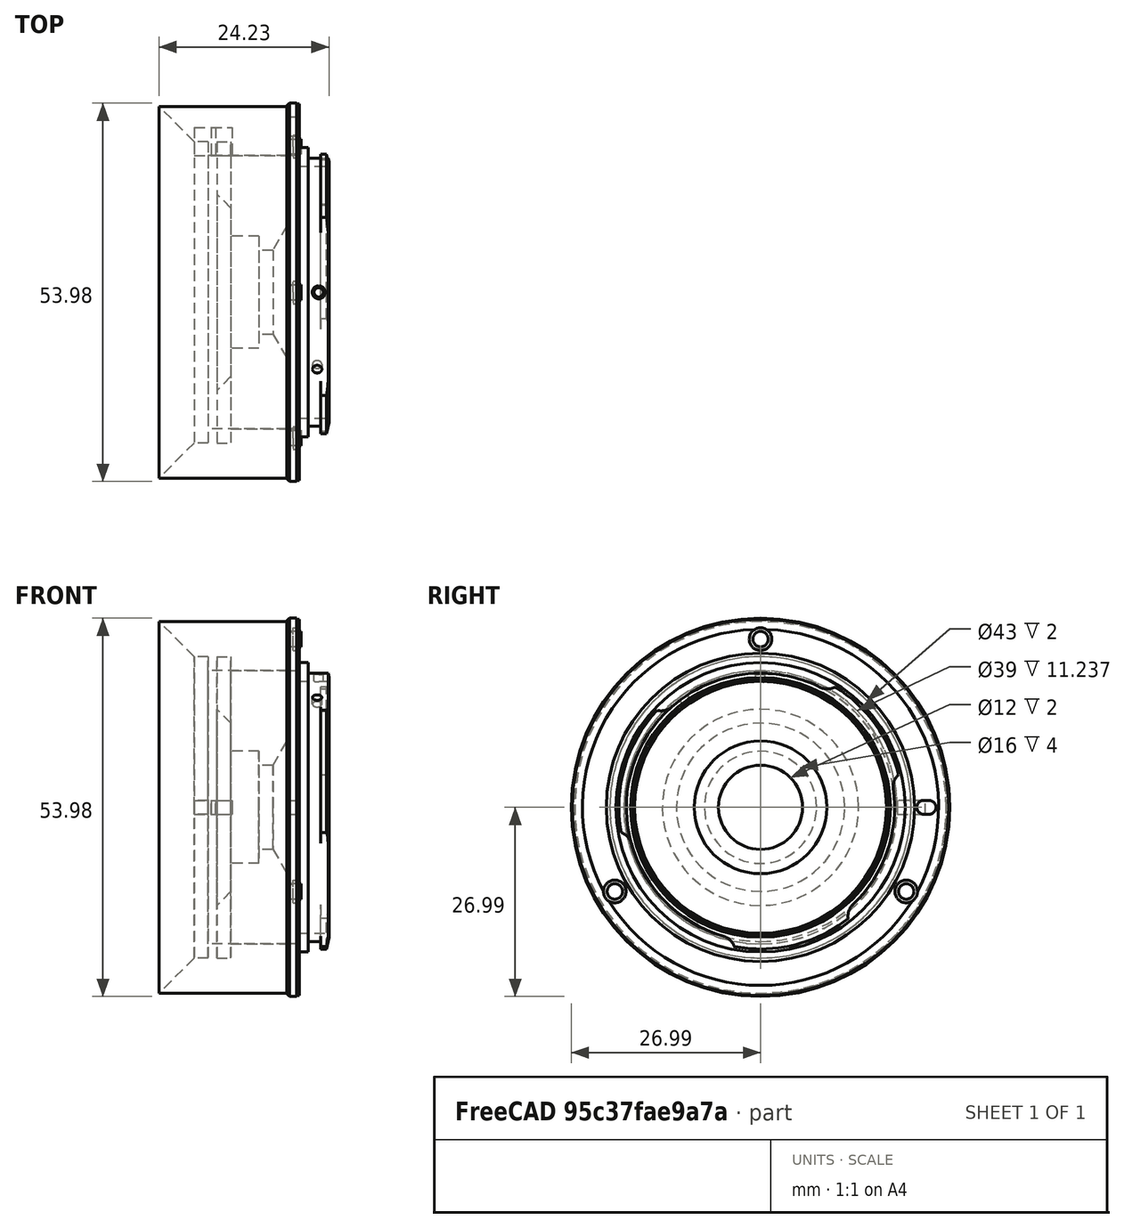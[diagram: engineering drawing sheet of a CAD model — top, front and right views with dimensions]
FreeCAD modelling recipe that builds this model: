
FCSTD DOCUMENT  (FreeCAD 0.20R29410 (Git))
Label: FUJIQUICKSNAP
License: All rights reserved
LicenseURL: http://en.wikipedia.org/wiki/All_rights_reserved
objects: TechDraw::DrawViewDimension×27, TechDraw::DrawProjGroupItem×6, TechDraw::DrawHatch×6, Sketcher::SketchObject×5, PartDesign::Body×4, PartDesign::Pad×3, PartDesign::Revolution×2, PartDesign::Boolean×2, App::Part×2, TechDraw::DrawProjGroup×2, TechDraw::DrawViewSection×2, TechDraw::DrawViewAnnotation×2, Spreadsheet::Sheet×1, Part::Feature×1, TechDraw::DrawSVGTemplate×1, TechDraw::DrawViewSpreadsheet×1, TechDraw::DrawPage×1
note: 22 computed .brp shape members not serialized (recipe doc carries the construction recipe); baked Part::Feature solids carry a one-line shape summary decoded from their .brp

FEATURE [Spreadsheet::Sheet] Spreadsheet
  cells = A2=Focal length; B2(f)=32; C2=Mount inner radius; D2(MIR)==19.5mm; A3=Aperture; B3(Fstop)=10; C3=Mount outer radius; D3(MOR)==26.5mm; A4=Hyperfocal; B4(HFD)==B2 ^ 2 / (B3 / 30); C4=Lens support radius; D4(LSR)==8mm; A5=Lens to sensor; B5(L2S)==1 / (1 / B2 - 1 / B4); C5=Lens support depth; D5(LSD)==4mm; A6=FFD; B6(FFD)==19.25 + 1.85; A7=Mount to lens; B7(M2L)==B5 - B6
FEATURE [Sketcher::SketchObject] Sketch
  FullyConstrained = true
  MapMode = 5
  Support = -> [XY_Plane001]
  expr: Constraints[17] = Spreadsheet.M2L
  expr: Constraints[7] = Spreadsheet.MIR
  expr: Constraints[8] = Spreadsheet.MOR
  sketch-geometry (6):
    g0: LineSegment StartX=-18.2368 StartY=26.5 StartZ=0 EndX=0 EndY=26.5 EndZ=0
    g1: LineSegment StartX=0 StartY=26.5 StartZ=0 EndX=0 EndY=19.5 EndZ=0
    g2: LineSegment StartX=-13.2368 StartY=21.5 StartZ=0 EndX=-18.2368 EndY=26.5 EndZ=0
    g3: LineSegment StartX=0 StartY=19.5 StartZ=0 EndX=-11.2368 EndY=19.5 EndZ=0
    g4: LineSegment StartX=-11.2368 StartY=19.5 StartZ=0 EndX=-11.2368 EndY=21.5 EndZ=0
    g5: LineSegment StartX=-11.2368 StartY=21.5 StartZ=0 EndX=-13.2368 EndY=21.5 EndZ=0
  constraints (18):
    c: Coincident(g0,g1)
    c: Coincident(g1,g3)
    c: Coincident(g5,g2)
    c: Coincident(g2,g0)
    c: Horizontal(g0)
    c: Vertical(g1)
    c: PointOnObject(g1,g-2)
    c: DistanceY(g-1,g1) = 19.5
    c: DistanceY(g-1,g0) = 26.5
    c: Coincident(g3,g4)
    c: Horizontal(g3)
    c: Coincident(g4,g5)
    c: Horizontal(g5)
    c: Vertical(g4)
    c: Angle(g5,g2) = 2.35619
    c: Distance(g5) = 2
    c: Distance(g4) = 2
    c: DistanceX(g3,g1) = 11.2368
FEATURE [PartDesign::Revolution] Revolution
  Angle = 360
  Axis = (1,0,0)
  Base = (0,0,0)
  Profile = -> Sketch
  ReferenceAxis = -> Sketch [H_Axis]
FEATURE [Sketcher::SketchObject] Sketch001
  FullyConstrained = true
  MapMode = 5
  Support = -> [XY_Plane003]
  expr: Constraints[18] = Spreadsheet.MIR
  expr: Constraints[23] = Spreadsheet.LSR
  expr: Constraints[27] = Spreadsheet.LSD
  expr: Constraints[28] = Constraints[26] + Constraints[27]
  sketch-geometry (11):
    g0: LineSegment StartX=-8 StartY=19.5 StartZ=0 EndX=0 EndY=19.5 EndZ=0
    g1: LineSegment StartX=0 StartY=19.5 StartZ=0 EndX=0 EndY=9.4641 EndZ=0
    g2: LineSegment StartX=-8 StartY=21.5 StartZ=0 EndX=-8 EndY=19.5 EndZ=0
    g3: LineSegment StartX=-10 StartY=21.5 StartZ=0 EndX=-8 EndY=21.5 EndZ=0
    g4: LineSegment StartX=-10 StartY=14 StartZ=0 EndX=-10 EndY=21.5 EndZ=0
    g5: LineSegment StartX=-8 StartY=8 StartZ=0 EndX=-8 EndY=12 EndZ=0
    g6: LineSegment StartX=-8 StartY=12 StartZ=0 EndX=-10 EndY=14 EndZ=0
    g7: LineSegment StartX=-4 StartY=8 StartZ=0 EndX=-8 EndY=8 EndZ=0
    g8: LineSegment StartX=-4 StartY=6 StartZ=0 EndX=-4 EndY=8 EndZ=0
    g9: LineSegment StartX=0 StartY=9.4641 StartZ=0 EndX=-2 EndY=6 EndZ=0
    g10: LineSegment StartX=-2 StartY=6 StartZ=0 EndX=-4 EndY=6 EndZ=0
  constraints (33):
    c: Coincident(g0,g1)
    c: Coincident(g1,g9)
    c: Coincident(g7,g5)
    c: Coincident(g2,g0)
    c: Horizontal(g0)
    c: Vertical(g1)
    c: PointOnObject(g1,g-2)
    c: Coincident(g3,g2)
    c: Vertical(g2)
    c: Coincident(g4,g3)
    c: Horizontal(g3)
    c: DistanceY(g2,g2) = 2
    c: Coincident(g6,g4)
    c: Vertical(g4)
    c: Coincident(g5,g6)
    c: Vertical(g5)
    c: DistanceX(g3,g3) = 2
    c: Angle(g6,g4) = 2.35619
    c: DistanceY(g-1,g0) = 19.5
    c: DistanceY(g5,g5) = 4
    c: Coincident(g8,g7)
    c: Horizontal(g7)
    c: Coincident(g10,g8)
    c: DistanceY(g-1,g7) = 8
    c: Vertical(g8)
    c: DistanceY(g8,g8) = 2
    c: DistanceX(g10,g9) = 4
    c: DistanceX(g7,g7) = 4
    c: DistanceX(g0,g0) = 8
    c: Coincident(g9,g10)
    c: Horizontal(g10)
    c: Angle(g1,g9) = 2.61799
    c: DistanceX(g10,g10) = 2
FEATURE [PartDesign::Revolution] Revolution001
  Angle = 360
  Axis = (1,0,0)
  Base = (0,0,0)
  Profile = -> Sketch001
  ReferenceAxis = -> Sketch001 [H_Axis]
FEATURE [Part::Feature] Solid  label="u43 lens mount"
  Placement = pos=(0,0,0) rot=(0,0,1;4.71239rad)
  shape: bbox 5.994 x 53.98 x 53.98 mm, 69 faces (baked)
FEATURE [Sketcher::SketchObject] Sketch002
  FullyConstrained = true
  MapMode = 5
  Placement = pos=(0,0,0) rot=(0.57735,0.57735,0.57735;2.0944rad)
  Support = -> [YZ_Plane001]
  expr: Constraints[7] = 2 * 24 * cos(30)
  expr: Constraints[8] = 2 * 24 * cos(30)
  sketch-geometry (3):
    g0: Circle CenterX=-20.7846 CenterY=-12 CenterZ=0 NormalX=0 NormalY=0 NormalZ=1 AngleXU=0 Radius=1.1
    g1: Circle CenterX=20.7846 CenterY=-12 CenterZ=0 NormalX=0 NormalY=0 NormalZ=1 AngleXU=0 Radius=1.1
    g2: Circle CenterX=0 CenterY=24 CenterZ=0 NormalX=0 NormalY=0 NormalZ=1 AngleXU=0 Radius=1.1
  constraints (9):
    c: PointOnObject(g2,g-2)
    c: DistanceY(g-1,g2) = 24
    c: Radius(g0) = 1.1
    c: Equal(g0,g1)
    c: Equal(g1,g2)
    c: Distance(g-1,g0) = 24
    c: Distance(g-1,g1) = 24
    c: DistanceX(g0,g1) = 41.5692
    c: Distance(g1,g2) = 41.5692
FEATURE [PartDesign::Pad] Pad
  BaseFeature = -> Revolution
  Direction = (1,-2e-16,3e-16)
  Length = 2
  Length2 = 10
  Profile = -> Sketch002
  ReferenceAxis = -> Sketch002 [N_Axis]
  Type = 0
FEATURE [Sketcher::SketchObject] Sketch003
  FullyConstrained = true
  MapMode = 5
  Placement = pos=(0,0,0) rot=(0.57735,0.57735,0.57735;2.0944rad)
  Support = -> [YZ_Plane004]
  expr: Constraints[14] = Spreadsheet.MIR
  sketch-geometry (5):
    g0: LineSegment StartX=23.5 StartY=1 StartZ=0 EndX=19.5 EndY=1 EndZ=0
    g1: LineSegment StartX=19.5 StartY=-1 StartZ=0 EndX=23.5 EndY=-1 EndZ=0
    g2: LineSegment StartX=23.5 StartY=-1 StartZ=0 EndX=23.5 EndY=1 EndZ=0
    g3: LineSegment StartX=19.5 StartY=1 StartZ=0 EndX=19.5 EndY=0 EndZ=0
    g4: LineSegment StartX=19.5 StartY=0 StartZ=0 EndX=19.5 EndY=-1 EndZ=0
  constraints (15):
    c: Coincident(g0,g3)
    c: Coincident(g4,g1)
    c: Coincident(g1,g2)
    c: Coincident(g2,g0)
    c: Horizontal(g0)
    c: Horizontal(g1)
    c: Vertical(g2)
    c: Coincident(g3,g4)
    c: Vertical(g3)
    c: Vertical(g4)
    c: PointOnObject(g3,g-1)
    c: Equal(g3,g4)
    c: DistanceY(g2,g2) = 2
    c: DistanceX(g0,g0) = 4
    c: DistanceX(g-1,g3) = 19.5
FEATURE [PartDesign::Pad] Pad001
  Direction = (1,-2e-16,3e-16)
  Length = 3
  Length2 = 10
  Placement = pos=(0,0,0) rot=(0.57735,0.57735,0.57735;2.0944rad)
  Profile = -> Sketch003
  ReferenceAxis = -> Sketch003 [N_Axis]
  Type = 0
FEATURE [PartDesign::Body] Body002
  Group = -> [Sketch003,Pad001]
  Origin = -> Origin004
  Placement = pos=(-13.2,0,0) rot=(0,0,1;0rad)
  Tip = -> Pad001
FEATURE [Sketcher::SketchObject] Sketch004
  FullyConstrained = true
  MapMode = 5
  Placement = pos=(0,0,0) rot=(0.57735,0.57735,0.57735;2.0944rad)
  Support = -> [YZ_Plane005]
  expr: Constraints[14] = Spreadsheet.MIR
  sketch-geometry (5):
    g0: LineSegment StartX=23.5 StartY=1 StartZ=0 EndX=19.5 EndY=1 EndZ=0
    g1: LineSegment StartX=19.5 StartY=-1 StartZ=0 EndX=23.5 EndY=-1 EndZ=0
    g2: LineSegment StartX=23.5 StartY=-1 StartZ=0 EndX=23.5 EndY=1 EndZ=0
    g3: LineSegment StartX=19.5 StartY=1 StartZ=0 EndX=19.5 EndY=0 EndZ=0
    g4: LineSegment StartX=19.5 StartY=0 StartZ=0 EndX=19.5 EndY=-1 EndZ=0
  constraints (15):
    c: Coincident(g0,g3)
    c: Coincident(g4,g1)
    c: Coincident(g1,g2)
    c: Coincident(g2,g0)
    c: Horizontal(g0)
    c: Horizontal(g1)
    c: Vertical(g2)
    c: Coincident(g3,g4)
    c: Vertical(g3)
    c: Vertical(g4)
    c: PointOnObject(g3,g-1)
    c: Equal(g3,g4)
    c: DistanceY(g2,g2) = 2
    c: DistanceX(g0,g0) = 4
    c: DistanceX(g-1,g3) = 19.5
FEATURE [PartDesign::Pad] Pad002
  Direction = (1,-2e-16,3e-16)
  Length = 3
  Length2 = 10
  Placement = pos=(0,0,0) rot=(0.57735,0.57735,0.57735;2.0944rad)
  Profile = -> Sketch004
  ReferenceAxis = -> Sketch004 [N_Axis]
  Type = 0
FEATURE [PartDesign::Body] Body003
  Group = -> [Sketch004,Pad002]
  Origin = -> Origin005
  Placement = pos=(-10.8,0,0) rot=(0,0,1;0rad)
  Tip = -> Pad002
FEATURE [PartDesign::Boolean] Boolean
  BaseFeature = -> Pad
  Group = -> [Body002]
  Type = 0
FEATURE [PartDesign::Body] Body
  Group = -> [Sketch,Revolution,Sketch002,Pad,Boolean]
  Origin = -> Origin001
  Tip = -> Boolean
FEATURE [App::Part] Part  label="Tube"
  Group = -> [Body]
  Origin = -> Origin
FEATURE [PartDesign::Boolean] Boolean001
  BaseFeature = -> Revolution001
  Group = -> [Body003]
  Type = 1
FEATURE [PartDesign::Body] Body001
  Group = -> [Sketch001,Revolution001,Boolean001]
  Origin = -> Origin003
  Tip = -> Boolean001
FEATURE [App::Part] Part001  label="Cap"
  Group = -> [Body001]
  Origin = -> Origin002
  Placement = pos=(-3.3,0,0) rot=(0,0,1;0rad)
FEATURE [TechDraw::DrawSVGTemplate] Template
  EditableTexts = AUTHOR_NAME=monke; DN=1; DRAWING_TITLE=QUICKSNAP TO µ4/3; FC-DATE=17/09/2022; FC-REV=REV A; FC-SC=SCALE; FC-SH=1/1; FC-SI=A4; FreeCAD_DRAWING=1.85mm thick µ4/3 mount not included; PN=1; SI-1=Units in millimeter
  Height = 210
  Orientation = 1
  Width = 297
FEATURE [TechDraw::DrawProjGroupItem] ProjItem  label="Front"
  CoarseView = false
  Direction = (-1,0,0)
  Focus = 100
  HardHidden = false
  IsoCount = 0
  IsoHidden = false
  IsoVisible = false
  LockPosition = true
  Perspective = false
  Rotation = 0
  RotationVector = (0,1,0)
  ScaleType = 2
  SeamHidden = false
  SeamVisible = true
  SmoothHidden = false
  SmoothVisible = true
  Source = -> [Part001]
  Type = 0
  X = 0
  XDirection = (0,-1,2e-16)
  Y = 0
FEATURE [TechDraw::DrawProjGroupItem] ProjItem003  label="Bottom"
  CoarseView = false
  Direction = (0,-2e-16,-1)
  Focus = 100
  HardHidden = false
  IsoCount = 0
  IsoHidden = false
  IsoVisible = false
  LockPosition = false
  Perspective = false
  Rotation = 0
  RotationVector = (1,0,0)
  ScaleType = 2
  SeamHidden = false
  SeamVisible = true
  SmoothHidden = false
  SmoothVisible = true
  Source = -> [Part001]
  Type = 5
  X = 0
  XDirection = (0,-1,2e-16)
  Y = -48
FEATURE [TechDraw::DrawProjGroupItem] ProjItem004  label="Rear"
  CoarseView = false
  Direction = (1,0,0)
  Focus = 100
  HardHidden = false
  IsoCount = 0
  IsoHidden = false
  IsoVisible = false
  LockPosition = false
  Perspective = false
  Rotation = 0
  RotationVector = (1,0,0)
  ScaleType = 2
  SeamHidden = false
  SeamVisible = true
  SmoothHidden = false
  SmoothVisible = true
  Source = -> [Part001]
  Type = 3
  X = 47.9767
  XDirection = (0,1,-2e-16)
  Y = 0
FEATURE [TechDraw::DrawProjGroup] ProjGroup
  Anchor = -> ProjItem
  AutoDistribute = true
  LockPosition = false
  ProjectionType = 1
  Rotation = 0
  Scale = 1.5
  ScaleType = 0
  Source = -> [Part001]
  Views = -> [ProjItem,ProjItem003,ProjItem004]
  X = 41.5078
  Y = 159.868
  spacingX = 5
  spacingY = 5
FEATURE [TechDraw::DrawViewDimension] Dimension
  AngleOverride = false
  Arbitrary = false
  ArbitraryTolerances = false
  EqualTolerance = true
  ExtensionAngle = 0
  FormatSpec = ⌀%.2w
  FormatSpecOverTolerance = %+.2w
  FormatSpecUnderTolerance = %+.2w
  Inverted = false
  LineAngle = 0
  LockPosition = false
  MeasureType = 1
  OverTolerance = 0
  References2D = -> [ProjItem004]
  Rotation = 0
  ScaleType = 0
  TheoreticalExact = false
  Type = 5
  UnderTolerance = 0
  X = 10.6396
  Y = -6.61379
FEATURE [TechDraw::DrawViewDimension] Dimension001
  AngleOverride = false
  Arbitrary = false
  ArbitraryTolerances = false
  EqualTolerance = true
  ExtensionAngle = 0
  FormatSpec = ⌀%.2w
  FormatSpecOverTolerance = %+.2w
  FormatSpecUnderTolerance = %+.2w
  Inverted = false
  LineAngle = 0
  LockPosition = false
  MeasureType = 1
  OverTolerance = 0
  References2D = -> [ProjItem004]
  Rotation = 0
  ScaleType = 0
  TheoreticalExact = false
  Type = 5
  UnderTolerance = 0
  X = 28.1565
  Y = -4.45712
FEATURE [TechDraw::DrawViewDimension] Dimension002
  AngleOverride = false
  Arbitrary = false
  ArbitraryTolerances = false
  EqualTolerance = true
  ExtensionAngle = 0
  FormatSpec = ⌀%.2w
  FormatSpecOverTolerance = %+.2w
  FormatSpecUnderTolerance = %+.2w
  Inverted = false
  LineAngle = 0
  LockPosition = false
  MeasureType = 1
  OverTolerance = 0
  References2D = -> [ProjItem004]
  Rotation = 0
  ScaleType = 0
  TheoreticalExact = false
  Type = 5
  UnderTolerance = 0
  X = 10.5917
  Y = 26.4552
FEATURE [TechDraw::DrawViewDimension] Dimension003
  AngleOverride = false
  Arbitrary = false
  ArbitraryTolerances = false
  EqualTolerance = true
  ExtensionAngle = 0
  FormatSpec = ⌀%.2w
  FormatSpecOverTolerance = %+.2w
  FormatSpecUnderTolerance = %+.2w
  Inverted = false
  LineAngle = 0
  LockPosition = false
  MeasureType = 1
  OverTolerance = 0
  References2D = -> [ProjItem004]
  Rotation = 0
  ScaleType = 0
  TheoreticalExact = false
  Type = 5
  UnderTolerance = 0
  X = 18.3317
  Y = 23.0764
FEATURE [TechDraw::DrawViewDimension] Dimension004
  AngleOverride = false
  Arbitrary = false
  ArbitraryTolerances = false
  EqualTolerance = true
  ExtensionAngle = 0
  FormatSpec = %.2w
  FormatSpecOverTolerance = %+.2w
  FormatSpecUnderTolerance = %+.2w
  Inverted = false
  LineAngle = 0
  LockPosition = false
  MeasureType = 1
  OverTolerance = 0
  References2D = -> [ProjItem]
  Rotation = 0
  ScaleType = 0
  TheoreticalExact = false
  Type = 1
  UnderTolerance = 0
  X = -15.9193
  Y = 13.2354
FEATURE [TechDraw::DrawViewDimension] Dimension005
  AngleOverride = false
  Arbitrary = false
  ArbitraryTolerances = false
  EqualTolerance = true
  ExtensionAngle = 0
  FormatSpec = %.2w
  FormatSpecOverTolerance = %+.2w
  FormatSpecUnderTolerance = %+.2w
  Inverted = false
  LineAngle = 0
  LockPosition = false
  MeasureType = 1
  OverTolerance = 0
  References2D = -> [ProjItem]
  Rotation = 0
  ScaleType = 0
  TheoreticalExact = false
  Type = 1
  UnderTolerance = 0
  X = -3.54512
  Y = 21.0953
FEATURE [TechDraw::DrawViewDimension] Dimension006
  AngleOverride = false
  Arbitrary = false
  ArbitraryTolerances = false
  EqualTolerance = true
  ExtensionAngle = 0
  FormatSpec = %.2w
  FormatSpecOverTolerance = %+.2w
  FormatSpecUnderTolerance = %+.2w
  Inverted = false
  LineAngle = 0
  LockPosition = false
  MeasureType = 1
  OverTolerance = 0
  References2D = -> [ProjItem]
  Rotation = 0
  ScaleType = 0
  TheoreticalExact = false
  Type = 1
  UnderTolerance = 0
  X = -14.8124
  Y = -5.64743
FEATURE [TechDraw::DrawViewDimension] Dimension007
  AngleOverride = false
  Arbitrary = false
  ArbitraryTolerances = false
  EqualTolerance = true
  ExtensionAngle = 0
  FormatSpec = %.2w
  FormatSpecOverTolerance = %+.2w
  FormatSpecUnderTolerance = %+.2w
  Inverted = false
  LineAngle = 0
  LockPosition = false
  MeasureType = 1
  OverTolerance = 0
  References2D = -> [ProjItem003]
  Rotation = 0
  ScaleType = 0
  TheoreticalExact = false
  Type = 2
  UnderTolerance = 0
  X = -27.1178
  Y = 9.4377
FEATURE [TechDraw::DrawViewDimension] Dimension008
  AngleOverride = false
  Arbitrary = false
  ArbitraryTolerances = false
  EqualTolerance = true
  ExtensionAngle = 0
  FormatSpec = %.2w
  FormatSpecOverTolerance = %+.2w
  FormatSpecUnderTolerance = %+.2w
  Inverted = false
  LineAngle = 0
  LockPosition = false
  MeasureType = 1
  OverTolerance = 0
  References2D = -> [ProjItem003]
  Rotation = 0
  ScaleType = 0
  TheoreticalExact = false
  Type = 2
  UnderTolerance = 0
  X = -18.1561
  Y = -8.31386
FEATURE [TechDraw::DrawProjGroupItem] ProjItem005  label="Front001"
  CoarseView = false
  Direction = (1,0,0)
  Focus = 100
  HardHidden = false
  IsoCount = 0
  IsoHidden = false
  IsoVisible = false
  LockPosition = true
  Perspective = false
  Rotation = 0
  RotationVector = (0,1,0)
  ScaleType = 2
  SeamHidden = false
  SeamVisible = true
  SmoothHidden = false
  SmoothVisible = true
  Source = -> [Part]
  Type = 0
  X = 0
  XDirection = (0,1,0)
  Y = 0
FEATURE [TechDraw::DrawProjGroupItem] ProjItem007  label="Rear001"
  CoarseView = false
  Direction = (-1,0,0)
  Focus = 100
  HardHidden = false
  IsoCount = 0
  IsoHidden = false
  IsoVisible = false
  LockPosition = false
  Perspective = false
  Rotation = 0
  RotationVector = (1,0,0)
  ScaleType = 2
  SeamHidden = false
  SeamVisible = true
  SmoothHidden = false
  SmoothVisible = true
  Source = -> [Part]
  Type = 3
  X = 58
  XDirection = (0,-1,0)
  Y = 0
FEATURE [TechDraw::DrawProjGroupItem] ProjItem009  label="Bottom001"
  CoarseView = false
  Direction = (0,0,-1)
  Focus = 100
  HardHidden = false
  IsoCount = 0
  IsoHidden = false
  IsoVisible = false
  LockPosition = false
  Perspective = false
  Rotation = 0
  RotationVector = (1,0,0)
  ScaleType = 2
  SeamHidden = false
  SeamVisible = true
  SmoothHidden = false
  SmoothVisible = true
  Source = -> [Part]
  Type = 5
  X = 0
  XDirection = (0,1,0)
  Y = -58
FEATURE [TechDraw::DrawProjGroup] ProjGroup001
  Anchor = -> ProjItem005
  AutoDistribute = true
  LockPosition = false
  ProjectionType = 1
  Rotation = 0
  ScaleType = 0
  Source = -> [Part]
  Views = -> [ProjItem005,ProjItem007,ProjItem009]
  X = 194.711
  Y = 155.087
  spacingX = 5
  spacingY = 5
FEATURE [TechDraw::DrawViewDimension] Dimension009
  AngleOverride = false
  Arbitrary = false
  ArbitraryTolerances = false
  EqualTolerance = true
  ExtensionAngle = 0
  FormatSpec = %.2w
  FormatSpecOverTolerance = %+.2w
  FormatSpecUnderTolerance = %+.2w
  Inverted = false
  LineAngle = 0
  LockPosition = false
  MeasureType = 1
  OverTolerance = 0
  References2D = -> [ProjItem]
  Rotation = 0
  ScaleType = 0
  TheoreticalExact = false
  Type = 2
  UnderTolerance = 0
  X = -28.4985
  Y = 4.85505
FEATURE [TechDraw::DrawViewDimension] Dimension010
  AngleOverride = false
  Arbitrary = false
  ArbitraryTolerances = false
  EqualTolerance = true
  ExtensionAngle = 0
  FormatSpec = %.2w
  FormatSpecOverTolerance = %+.2w
  FormatSpecUnderTolerance = %+.2w
  Inverted = false
  LineAngle = 0
  LockPosition = false
  MeasureType = 1
  OverTolerance = 0
  References2D = -> [ProjItem004]
  Rotation = 0
  ScaleType = 0
  TheoreticalExact = false
  Type = 1
  UnderTolerance = 0
  X = 32.8498
  Y = 9.38181
FEATURE [TechDraw::DrawViewSection] SectionView  label="Section  - "
  BaseView = -> ProjItem003
  CoarseView = false
  CutSurfaceDisplay = 2
  Direction = (0,1,-2e-16)
  FileGeomPattern = <path>
  FileHatchPattern = <path>
  Focus = 100
  FuseBeforeCut = false
  HardHidden = false
  HatchScale = 1
  IsoCount = 0
  IsoHidden = false
  IsoVisible = false
  LockPosition = false
  NameGeomPattern = Diamond
  Perspective = false
  Rotation = 0
  ScaleType = 2
  SeamHidden = false
  SeamVisible = true
  SectionDirection = 0
  SectionNormal = (0,1,-2e-16)
  SectionOrigin = (-8.28,0.004,0)
  SmoothHidden = false
  SmoothVisible = true
  Source = -> [Part001]
  X = 92.1022
  XDirection = (0,-2e-16,-1)
  Y = 111.957
FEATURE [TechDraw::DrawViewDimension] Dimension011
  AngleOverride = false
  Arbitrary = false
  ArbitraryTolerances = false
  EqualTolerance = true
  ExtensionAngle = 0
  FormatSpec = %.2w
  FormatSpecOverTolerance = %+.2w
  FormatSpecUnderTolerance = %+.2w
  Inverted = false
  LineAngle = 0
  LockPosition = false
  MeasureType = 1
  OverTolerance = 0
  References2D = -> [SectionView]
  Rotation = 0
  ScaleType = 0
  TheoreticalExact = false
  Type = 2
  UnderTolerance = 0
  X = 24.5716
  Y = 2.73729
FEATURE [TechDraw::DrawViewDimension] Dimension012
  AngleOverride = false
  Arbitrary = false
  ArbitraryTolerances = false
  EqualTolerance = true
  ExtensionAngle = 0
  FormatSpec = %.2w
  FormatSpecOverTolerance = %+.2w
  FormatSpecUnderTolerance = %+.2w
  Inverted = false
  LineAngle = 0
  LockPosition = false
  MeasureType = 1
  OverTolerance = 0
  References2D = -> [SectionView]
  Rotation = 0
  ScaleType = 0
  TheoreticalExact = false
  Type = 2
  UnderTolerance = 0
  X = -13.5603
  Y = -5.56588
FEATURE [TechDraw::DrawViewDimension] Dimension013
  AngleOverride = false
  Arbitrary = false
  ArbitraryTolerances = false
  EqualTolerance = true
  ExtensionAngle = 0
  FormatSpec = %.2w
  FormatSpecOverTolerance = %+.2w
  FormatSpecUnderTolerance = %+.2w
  Inverted = false
  LineAngle = 0
  LockPosition = false
  MeasureType = 1
  OverTolerance = 0
  References2D = -> [SectionView]
  Rotation = 0
  ScaleType = 0
  TheoreticalExact = false
  Type = 6
  UnderTolerance = 0
  X = 8.91424
  Y = 14.234
FEATURE [TechDraw::DrawViewDimension] Dimension014
  AngleOverride = false
  Arbitrary = false
  ArbitraryTolerances = false
  EqualTolerance = true
  ExtensionAngle = 0
  FormatSpec = %.2w
  FormatSpecOverTolerance = %+.2w
  FormatSpecUnderTolerance = %+.2w
  Inverted = false
  LineAngle = 0
  LockPosition = false
  MeasureType = 1
  OverTolerance = 0
  References2D = -> [SectionView]
  Rotation = 0
  ScaleType = 0
  TheoreticalExact = false
  Type = 6
  UnderTolerance = 0
  X = 6.48562
  Y = -5.26713
FEATURE [TechDraw::DrawViewSection] SectionView001  label="Section  - 001"
  BaseView = -> ProjItem009
  CoarseView = false
  CutSurfaceDisplay = 2
  Direction = (0,1,0)
  FileGeomPattern = <path>
  FileHatchPattern = <path>
  Focus = 100
  FuseBeforeCut = false
  HardHidden = false
  HatchScale = 1
  IsoCount = 0
  IsoHidden = false
  IsoVisible = false
  LockPosition = false
  NameGeomPattern = Diamond
  Perspective = false
  Rotation = 0
  ScaleType = 2
  SeamHidden = false
  SeamVisible = true
  SectionDirection = 1
  SectionNormal = (0,1,0)
  SectionOrigin = (-8.17,0,0)
  SmoothHidden = false
  SmoothVisible = true
  Source = -> [Part]
  X = 252.71
  XDirection = (0,0,1)
  Y = 97.0634
FEATURE [TechDraw::DrawViewDimension] Dimension015
  AngleOverride = false
  Arbitrary = false
  ArbitraryTolerances = false
  EqualTolerance = true
  ExtensionAngle = 0
  FormatSpec = ⌀%.2w
  FormatSpecOverTolerance = %+.2w
  FormatSpecUnderTolerance = %+.2w
  Inverted = false
  LineAngle = 0
  LockPosition = false
  MeasureType = 1
  OverTolerance = 0
  References2D = -> [ProjItem005]
  Rotation = 0
  ScaleType = 0
  TheoreticalExact = false
  Type = 5
  UnderTolerance = 0
  X = -18.2039
  Y = 31.5677
FEATURE [TechDraw::DrawViewDimension] Dimension016
  AngleOverride = false
  Arbitrary = false
  ArbitraryTolerances = false
  EqualTolerance = true
  ExtensionAngle = 0
  FormatSpec = ⌀%.2w
  FormatSpecOverTolerance = %+.2w
  FormatSpecUnderTolerance = %+.2w
  Inverted = false
  LineAngle = 0
  LockPosition = false
  MeasureType = 1
  OverTolerance = 0
  References2D = -> [ProjItem005]
  Rotation = 0
  ScaleType = 0
  TheoreticalExact = false
  Type = 5
  UnderTolerance = 0
  X = 10.8696
  Y = 5.69361
FEATURE [TechDraw::DrawViewDimension] Dimension017
  AngleOverride = false
  Arbitrary = false
  ArbitraryTolerances = false
  EqualTolerance = true
  ExtensionAngle = 0
  FormatSpec = ⌀%.2w
  FormatSpecOverTolerance = %+.2w
  FormatSpecUnderTolerance = %+.2w
  Inverted = false
  LineAngle = 0
  LockPosition = false
  MeasureType = 1
  OverTolerance = 0
  References2D = -> [ProjItem005]
  Rotation = 0
  ScaleType = 0
  TheoreticalExact = false
  Type = 5
  UnderTolerance = 0
  X = -33.1265
  Y = -6.38375
FEATURE [TechDraw::DrawViewDimension] Dimension018
  AngleOverride = false
  Arbitrary = false
  ArbitraryTolerances = false
  EqualTolerance = true
  ExtensionAngle = 0
  FormatSpec = %.2w
  FormatSpecOverTolerance = %+.2w
  FormatSpecUnderTolerance = %+.2w
  Inverted = false
  LineAngle = 0
  LockPosition = false
  MeasureType = 1
  OverTolerance = 0
  References2D = -> [ProjItem007]
  Rotation = 0
  ScaleType = 0
  TheoreticalExact = false
  Type = 1
  UnderTolerance = 0
  X = -23.9507
  Y = -18.5146
FEATURE [TechDraw::DrawViewDimension] Dimension019
  AngleOverride = false
  Arbitrary = false
  ArbitraryTolerances = false
  EqualTolerance = true
  ExtensionAngle = 0
  FormatSpec = %.2w
  FormatSpecOverTolerance = %+.2w
  FormatSpecUnderTolerance = %+.2w
  Inverted = false
  LineAngle = 0
  LockPosition = false
  MeasureType = 1
  OverTolerance = 0
  References2D = -> [ProjItem009]
  Rotation = 0
  ScaleType = 0
  TheoreticalExact = false
  Type = 2
  UnderTolerance = 0
  X = -32.8837
  Y = 0.857026
FEATURE [TechDraw::DrawViewDimension] Dimension020
  AngleOverride = false
  Arbitrary = false
  ArbitraryTolerances = false
  EqualTolerance = true
  ExtensionAngle = 0
  FormatSpec = %.2w
  FormatSpecOverTolerance = %+.2w
  FormatSpecUnderTolerance = %+.2w
  Inverted = false
  LineAngle = 0
  LockPosition = false
  MeasureType = 1
  OverTolerance = 0
  References2D = -> [ProjItem009]
  Rotation = 0
  ScaleType = 0
  TheoreticalExact = false
  Type = 2
  UnderTolerance = 0
  X = -19.6258
  Y = 14.8707
FEATURE [TechDraw::DrawViewDimension] Dimension021
  AngleOverride = false
  Arbitrary = false
  ArbitraryTolerances = false
  EqualTolerance = true
  ExtensionAngle = 0
  FormatSpec = %.2w
  FormatSpecOverTolerance = %+.2w
  FormatSpecUnderTolerance = %+.2w
  Inverted = false
  LineAngle = 0
  LockPosition = false
  MeasureType = 1
  OverTolerance = 0
  References2D = -> [SectionView001]
  Rotation = 0
  ScaleType = 0
  TheoreticalExact = false
  Type = 6
  UnderTolerance = 0
  X = -21.0675
  Y = -11.1827
FEATURE [TechDraw::DrawViewDimension] Dimension022
  AngleOverride = false
  Arbitrary = false
  ArbitraryTolerances = false
  EqualTolerance = true
  ExtensionAngle = 0
  FormatSpec = %.2w
  FormatSpecOverTolerance = %+.2w
  FormatSpecUnderTolerance = %+.2w
  Inverted = false
  LineAngle = 0
  LockPosition = false
  MeasureType = 1
  OverTolerance = 0
  References2D = -> [SectionView001]
  Rotation = 0
  ScaleType = 0
  TheoreticalExact = false
  Type = 2
  UnderTolerance = 0
  X = 29.0921
  Y = -11.7082
FEATURE [TechDraw::DrawViewDimension] Dimension023
  AngleOverride = false
  Arbitrary = false
  ArbitraryTolerances = false
  EqualTolerance = true
  ExtensionAngle = 0
  FormatSpec = %.2w
  FormatSpecOverTolerance = %+.2w
  FormatSpecUnderTolerance = %+.2w
  Inverted = false
  LineAngle = 0
  LockPosition = false
  MeasureType = 1
  OverTolerance = 0
  References2D = -> [SectionView001]
  Rotation = 0
  ScaleType = 0
  TheoreticalExact = false
  Type = 2
  UnderTolerance = 0
  X = 14.0116
  Y = -5.91179
FEATURE [TechDraw::DrawViewDimension] Dimension024
  AngleOverride = false
  Arbitrary = false
  ArbitraryTolerances = false
  EqualTolerance = true
  ExtensionAngle = 0
  FormatSpec = %.2w
  FormatSpecOverTolerance = %+.2w
  FormatSpecUnderTolerance = %+.2w
  Inverted = false
  LineAngle = 0
  LockPosition = false
  MeasureType = 1
  OverTolerance = 0
  References2D = -> [SectionView001]
  Rotation = 0
  ScaleType = 0
  TheoreticalExact = false
  Type = 2
  UnderTolerance = 0
  X = -2.42635
  Y = 4.30108
FEATURE [TechDraw::DrawViewDimension] Dimension025
  AngleOverride = false
  Arbitrary = false
  ArbitraryTolerances = false
  EqualTolerance = true
  ExtensionAngle = 0
  FormatSpec = %.2w
  FormatSpecOverTolerance = %+.2w
  FormatSpecUnderTolerance = %+.2w
  Inverted = false
  LineAngle = 0
  LockPosition = false
  MeasureType = 1
  OverTolerance = 0
  References2D = -> [ProjItem007]
  Rotation = 0
  ScaleType = 0
  TheoreticalExact = false
  Type = 2
  UnderTolerance = 0
  X = -14.8847
  Y = 4.52196
FEATURE [TechDraw::DrawViewDimension] Dimension026
  AngleOverride = false
  Arbitrary = false
  ArbitraryTolerances = false
  EqualTolerance = true
  ExtensionAngle = 0
  FormatSpec = %.2w
  FormatSpecOverTolerance = %+.2w
  FormatSpecUnderTolerance = %+.2w
  Inverted = false
  LineAngle = 0
  LockPosition = false
  MeasureType = 1
  OverTolerance = 0
  References2D = -> [SectionView]
  Rotation = 0
  ScaleType = 0
  TheoreticalExact = false
  Type = 2
  UnderTolerance = 0
  X = -21.1803
  Y = 12.3386
FEATURE [TechDraw::DrawHatch] Hatch  label="HatchF1"
  HatchPattern = <path>
  Source = -> ProjItem007 [Face1,Face3]
FEATURE [TechDraw::DrawHatch] Hatch001  label="Hatch001F0"
  HatchPattern = <path>
  Source = -> ProjItem005 [Face0]
FEATURE [TechDraw::DrawHatch] Hatch002  label="Hatch002F2"
  HatchPattern = <path>
  Source = -> ProjItem004 [Face2,Face1,Face4]
FEATURE [TechDraw::DrawHatch] Hatch003  label="Hatch003F0"
  HatchPattern = <path>
  Source = -> ProjItem [Face0,Face2,Face3,Face4]
FEATURE [TechDraw::DrawHatch] Hatch004  label="Hatch004F1"
  HatchPattern = <path>
  Source = -> ProjItem003 [Face1,Face2]
FEATURE [TechDraw::DrawHatch] Hatch005  label="Hatch005F1"
  HatchPattern = <path>
  Source = -> ProjItem009 [Face1,Face4,Face3,Face2]
FEATURE [TechDraw::DrawViewAnnotation] Annotation
  Font = osifont
  LineSpace = 80
  LockPosition = false
  MaxWidth = -1
  Rotation = 0
  ScaleType = 0
  Text = Body Tube
  TextSize = 5
  TextStyle = 0
  X = 225.576
  Y = 69.7278
FEATURE [TechDraw::DrawViewAnnotation] Annotation001
  Font = osifont
  LineSpace = 80
  LockPosition = false
  MaxWidth = -1
  Rotation = 0
  ScaleType = 0
  Text = Lens Holding Cap
  TextSize = 5
  TextStyle = 0
  X = 64.5653
  Y = 88.3437
FEATURE [TechDraw::DrawViewSpreadsheet] Sheet
  CellEnd = D7
  CellStart = A2
  Font = osifont
  LineWidth = 1
  LockPosition = false
  Rotation = 0
  ScaleType = 2
  Source = -> Spreadsheet
  Symbol = <blob: 4914 chars omitted>
  TextSize = 12
  X = 58.2619
  Y = 36.884
FEATURE [TechDraw::DrawPage] Page
  KeepUpdated = true
  NextBalloonIndex = 1
  ProjectionType = 0
  Template = -> Template
  Views = -> [ProjGroup,Dimension,Dimension001,Dimension002,Dimension003,Dimension004,Dimension005,Dimension006,Dimension007,Dimension008,ProjGroup001,Dimension009,Dimension010,SectionView,Dimension011,Dimension012,Dimension013,Dimension014,SectionView001,Dimension015,Dimension016,Dimension017,Dimension018,Dimension019,Dimension020,Dimension021,Dimension022,Dimension023,Dimension024,Dimension025,Dimension026,+3 more]
note: 10 file-system paths scrubbed to <path> (originals preserved in the JSON sidecar)
